# Revit family: CCTYP01
name_source: partatom
category: Furniture
units: mm (PartAtom-declared; Revit-internal decimal feet)

## family parameters
Always vertical = Yes
Cut with Voids When Loaded = No
OmniClass Number = 23.40.20.00
OmniClass Title = General Furniture and Specialties
Render Appearance Source = Family Geometry
Room Calculation Point = No
Shared = No
Work Plane-Based = No

## types (1)
- CCTYP01
    Cost = 19450 $
    Default Elevation = 0 mm  [stored 0 ft]
    Description = 1 x Bolton High Back - Black Mesh Back - Black Seat Fabric, 1 x Devens Black Side Chair Express, 1 x Wall Mounted Open Overhead -16Hx60Wx14D, 1 x Table Desk, Rectangular, 2mm, O-Leg, 30Dx66Wx29H, 1 x WORKSURFACE RECT 24"D X 90"W X 1 1/8"TH, 1 x CBX Full Depth Floor Bookcase 24Dx21Hx30W, 1 x CBX Single Door Locker Right 66h x 12w x 24d, 2 x Cbx Full Depth Lat Bf 24dx21hx30w, 1 x Cbx Tackboard Wall Mount 45hx30w, 1 x Cbx Tackboard Wall Mount 28hx60w
    Exported From CET Designer = Yes
    Manufacturer = AIS
    Model = 4400
    Show CCTYP01 = Yes
    VisibilityIndex = 0

note: [stored X ft] marks values corroborated as IEEE doubles in the binary element streams (Revit-internal decimal feet)

## geometry (parser evidence)
native form markers: Sweep x3
no freeform markers — native parametric forms only
